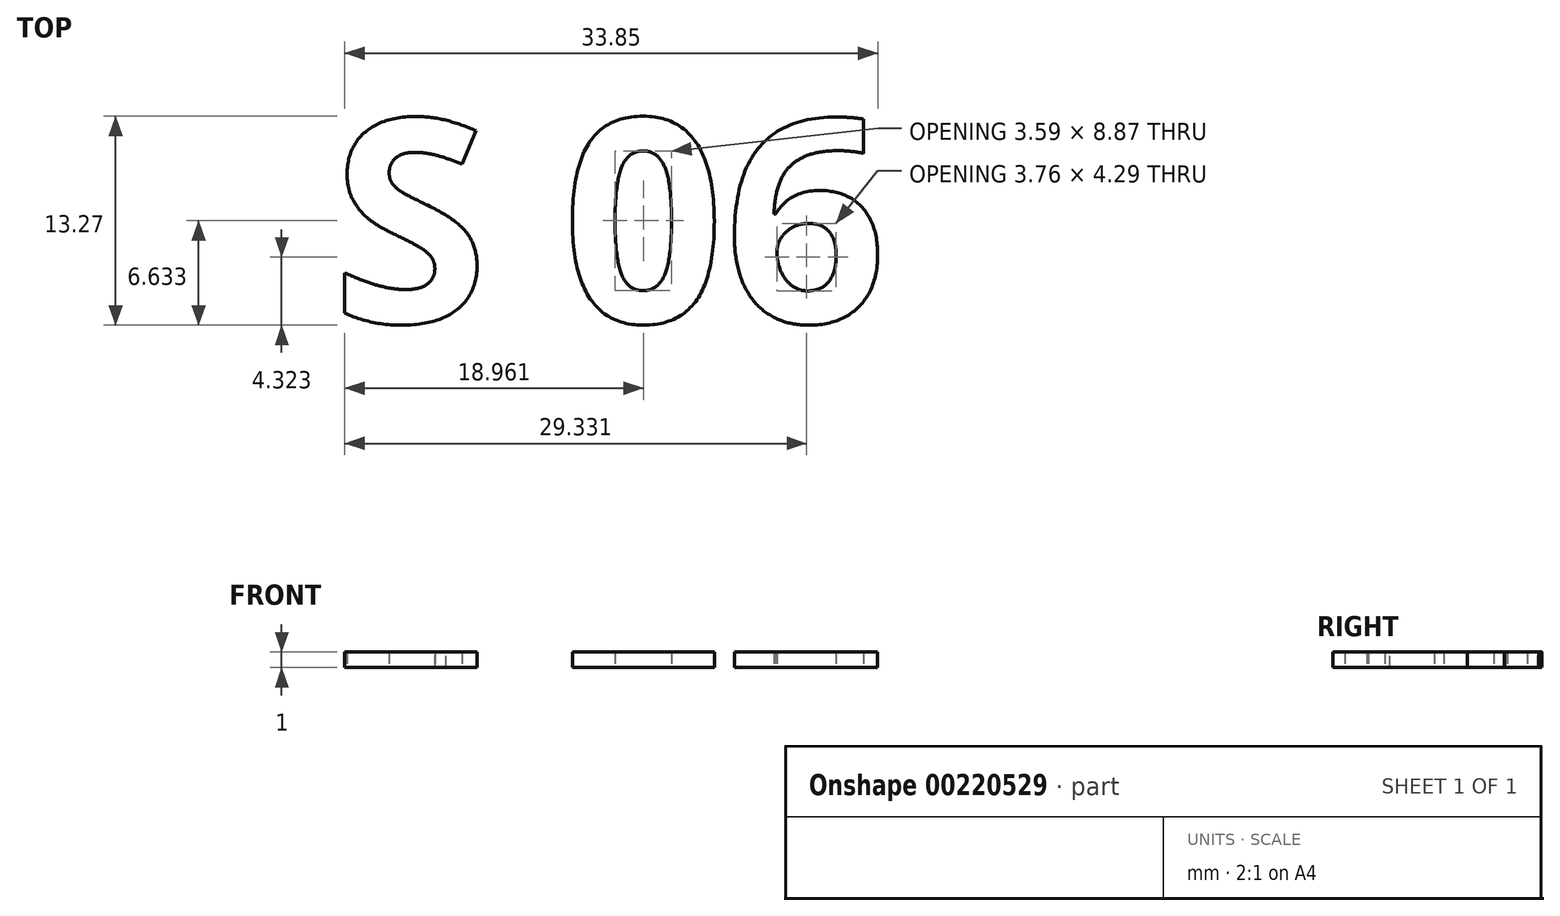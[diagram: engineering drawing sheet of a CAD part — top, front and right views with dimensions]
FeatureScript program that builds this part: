
annotation { "Feature Type Name" : "Feature", "Feature Type Description" : "" }
export const myFeature = defineFeature(function(context is Context, id is Id, definition is map)
    precondition{}
    {
        {
            var Q0;
            Q0=qCreatedBy(makeId("Top.planeOp"),FACE);
            var sketch = newSketch(context, id + "F0", { "sketchPlane" : qUnion([Q0])});
            skText(sketch, "E0", { "text": "S 06", "fontName": "OpenSans-Bold.ttf"});
            const initialGuessF0  = {"E0": [-0.01792, -0.0065, 1, 0, 0.013]};
            skSetInitialGuess(sketch, initialGuessF0);
            skSolve(sketch);
        }
        {
            var Q0;
            Q0=qSketchRegion(id+"F0",true);
            extrude(context, id + "F1", {"entities" : qUnion([Q0]), "depth" : 1 * mm});
        }
    });
